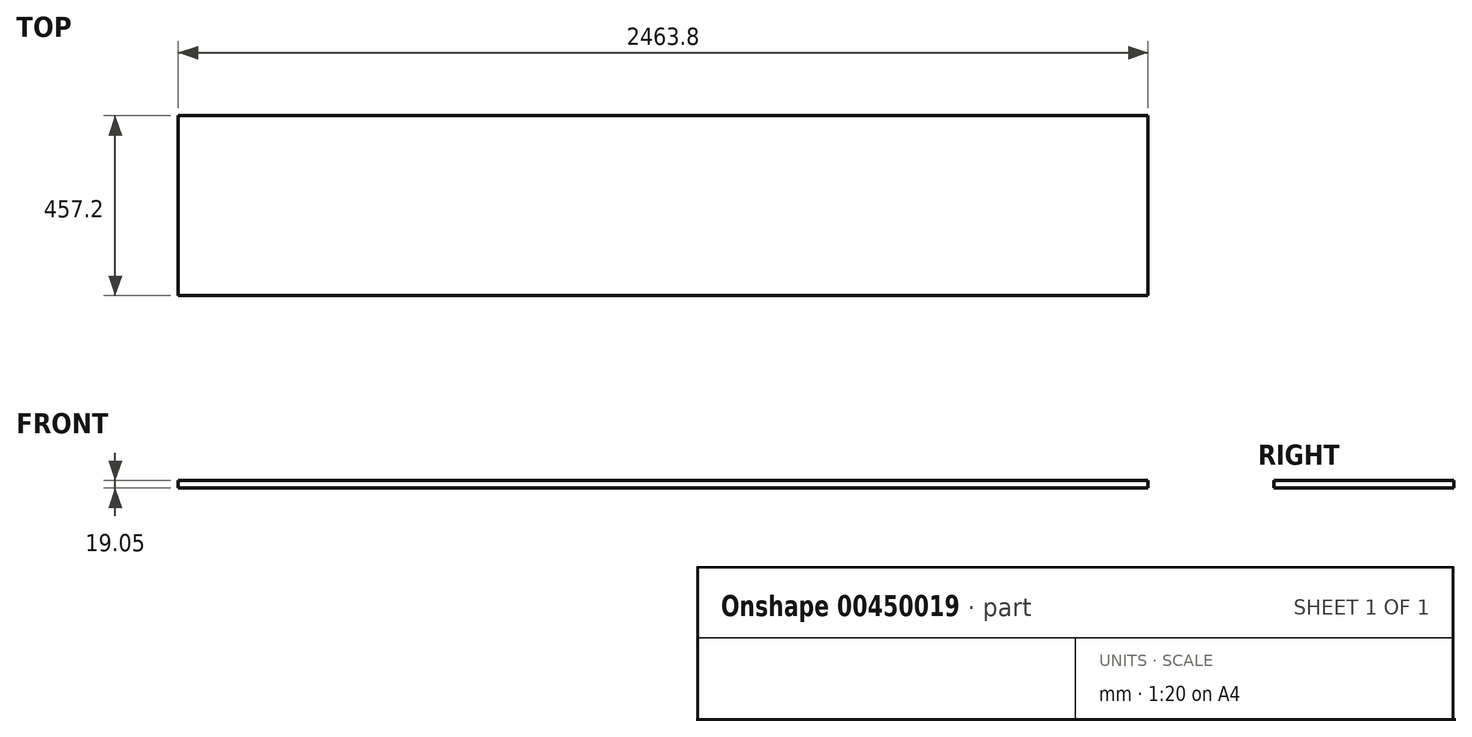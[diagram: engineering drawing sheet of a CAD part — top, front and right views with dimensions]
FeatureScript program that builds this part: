
annotation { "Feature Type Name" : "Feature", "Feature Type Description" : "" }
export const myFeature = defineFeature(function(context is Context, id is Id, definition is map)
    precondition{}
    {
        {
            var Q0;
            Q0=qCreatedBy(makeId("Top.planeOp"),FACE);
            var sketch = newSketch(context, id + "F0", { "sketchPlane" : qUnion([Q0])});
            skLineSegment(sketch, "E0", {"start": v(0, 0) * mm, "end": v(0, 119.1) * mm, "construction": true});
            skLineSegment(sketch, "E1", {"start": v(0, 0) * mm, "end": v(2463.8, 0) * mm, "construction": true});
            skLineSegment(sketch, "E2.bottom", {"start": v(0, 228.6) * mm, "end": v(2463.8, 228.6) * mm});
            skLineSegment(sketch, "E2.top", {"start": v(0, -228.6) * mm, "end": v(2463.8, -228.6) * mm});
            skLineSegment(sketch, "E2.left", {"start": v(0, 228.6) * mm, "end": v(0, -228.6) * mm});
            skLineSegment(sketch, "E2.right", {"start": v(2463.8, 228.6) * mm, "end": v(2463.8, -228.6) * mm});
            skSolve(sketch);
        }
        {
            var Q0;
            Q0=makeQuery(id+"F0.imprint","IMPRINT",FACE,{"disambiguationData":[TD([[makeQuery(id+"F0.imprint","IMPRINT",EDGE,{"derivedFrom":sQuery(id+"F0.wireOp",EDGE,"E2.bottom")}),-1.0]])]});
            extrude(context, id + "F1", {"entities" : qUnion([Q0]), "depth" : 19.05 * mm});
        }
    });
